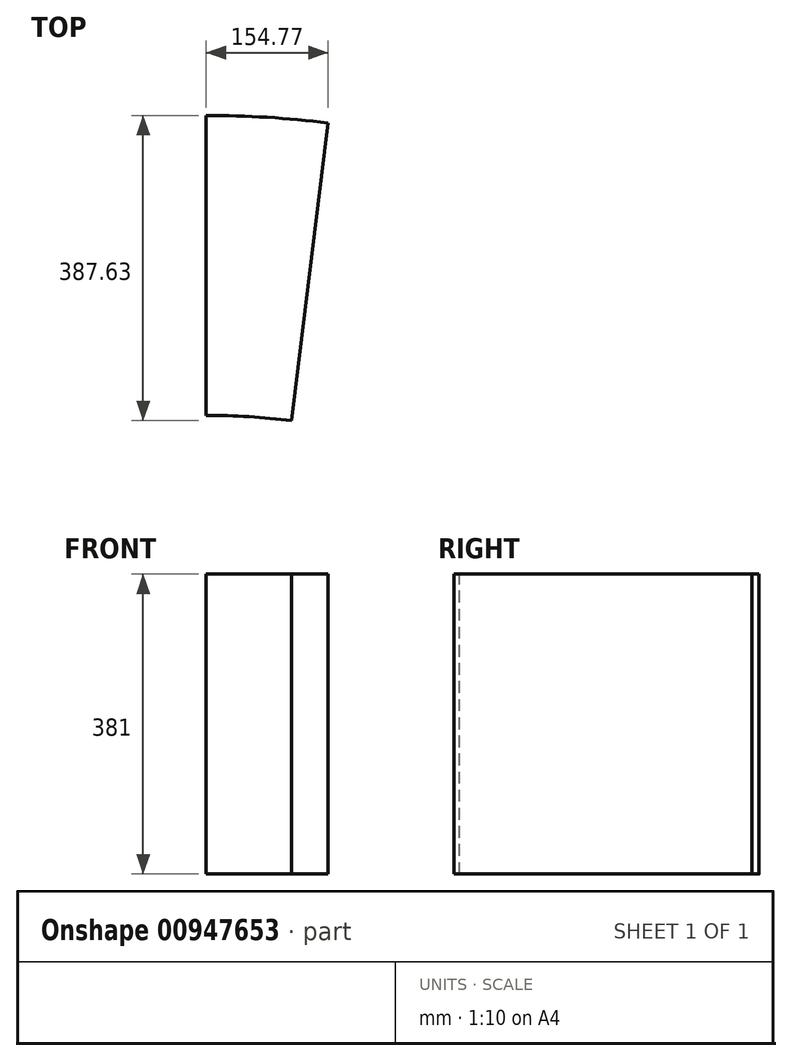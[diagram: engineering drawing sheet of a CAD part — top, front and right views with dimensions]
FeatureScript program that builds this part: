
annotation { "Feature Type Name" : "Feature", "Feature Type Description" : "" }
export const myFeature = defineFeature(function(context is Context, id is Id, definition is map)
    precondition{}
    {
        {
            var Q0;
            Q0=qCreatedBy(makeId("Top.planeOp"),FACE);
            var sketch = newSketch(context, id + "F0", { "sketchPlane" : qUnion([Q0])});
            skCircle(sketch, "E0", {"center": v(0, 0) * mm, "radius": 1270 * mm});
            skCircle(sketch, "E1", {"center": v(0, 0) * mm, "radius": 889 * mm});
            skSolve(sketch);
        }
        {
            var Q0;
            Q0=qCreatedBy(makeId("Top.planeOp"),FACE);
            var sketch = newSketch(context, id + "F1", { "sketchPlane" : qUnion([Q0])});
            skArc(sketch, "E2.0", {"start": v(154.77, 1260.53) * mm, "mid": v(77.53, 1267.63) * mm, "end": v(0, 1270) * mm});
            skArc(sketch, "E3.0", {"start": v(108.34, 882.37) * mm, "mid": v(54.27, 887.34) * mm, "end": v(0, 889) * mm});
            skLineSegment(sketch, "E4", {"start": v(0, 1270) * mm, "end": v(0, 889) * mm});
            skLineSegment(sketch, "E5", {"start": v(108.34, 882.37) * mm, "end": v(154.77, 1260.53) * mm});
            skSolve(sketch);
        }
        {
            var Q0;
            Q0 = qSketchRegion(id + "F1", true);
            extrude(context, id + "F2", {"entities" : qUnion([Q0]), "oppositeDirection" : true, "depth" : 381 * mm, "offsetDistance" : 25.4 * mm});
        }
    });
